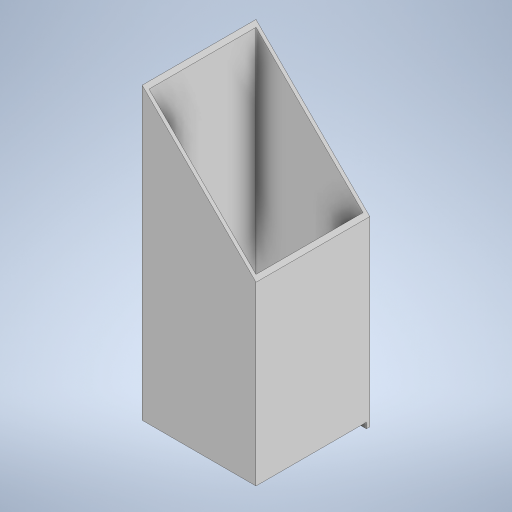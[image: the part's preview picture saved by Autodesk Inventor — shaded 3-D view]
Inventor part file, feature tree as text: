
AUTODESK INVENTOR PART (.ipt)
format: ipt  version: 2024.3 (Build 283343000, 343)  size: 249,856 bytes
history: native  units: mm
features: extrude x3, sketch x3, projected_geometry x2
ambient origin geometry x8: Origin, YZ Plane, XZ Plane, XY Plane, X Axis, Y Axis, Z Axis, Center Point
bodies: Solid1 (feature_tree)
feature tree (8):
  extrude  "Extrusion1"  Depth=3.0mm
  extrude  "Extrusion2"  Depth=100.0mm
  extrude  "Extrusion3"  TaperAngle=45.0deg  [1 undecoded]
  sketch  "Sketch1"  dims[d0=3.0mm d1=3.0mm]
  sketch  "Sketch2"  dims[d2=100.0mm d3=100.0mm]
  projected_geometry  "Projected Loop1"
  sketch  "Sketch3"  dims[d4=255.0mm d5=0.0mm d6=45.0deg d7=0.0mm d8=0.0mm d9=10.0mm d10=3.0mm d11=25.0mm d12=5.0mm d13=0.0mm]
  projected_geometry  "Projected Loop2"
note: 1 required parameter value undecoded (feature->parameter linkage not recoverable at this tier; creation-order binding heuristic only, values carry confidence <= 0.55)
